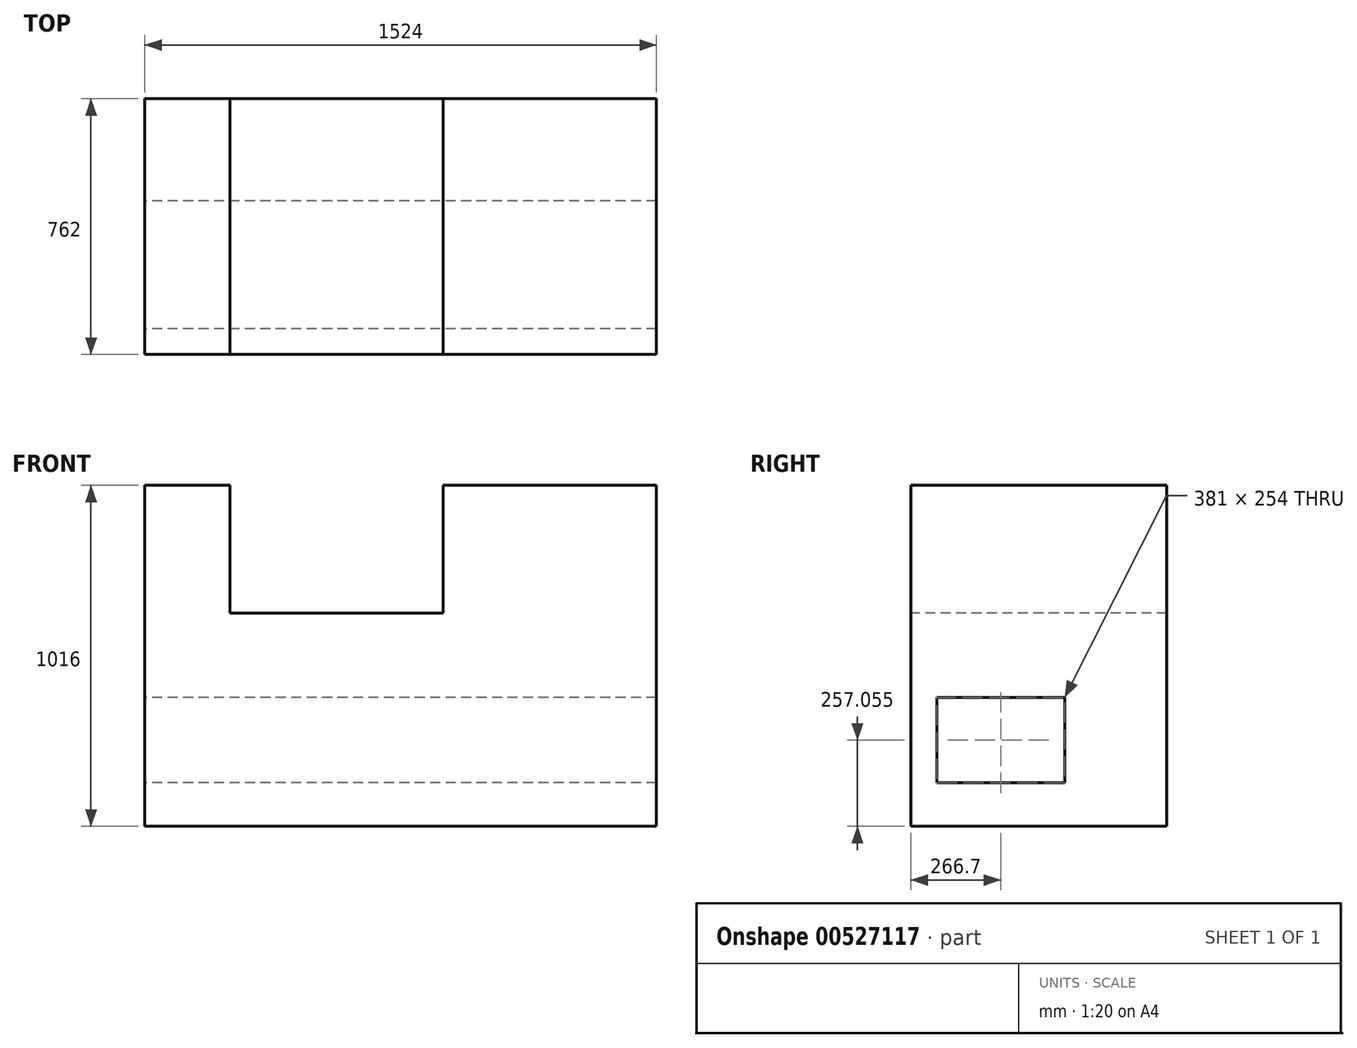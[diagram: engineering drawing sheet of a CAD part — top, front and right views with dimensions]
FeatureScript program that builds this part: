
annotation { "Feature Type Name" : "Feature", "Feature Type Description" : "" }
export const myFeature = defineFeature(function(context is Context, id is Id, definition is map)
    precondition{}
    {
        {
            var Q0;
            Q0=qCreatedBy(makeId("Right.planeOp"),FACE);
            var sketch = newSketch(context, id + "F0", { "sketchPlane" : qUnion([Q0])});
            skLineSegment(sketch, "E0.bottom", {"start": v(-457.2, 536.01) * mm, "end": v(304.8, 536.01) * mm});
            skLineSegment(sketch, "E0.top", {"start": v(-457.2, -479.99) * mm, "end": v(304.8, -479.99) * mm});
            skLineSegment(sketch, "E0.left", {"start": v(-457.2, 536.01) * mm, "end": v(-457.2, -479.99) * mm});
            skLineSegment(sketch, "E0.right", {"start": v(304.8, 536.01) * mm, "end": v(304.8, -479.99) * mm});
            skLineSegment(sketch, "E1.bottom", {"start": v(-381, -349.94) * mm, "end": v(0, -349.94) * mm});
            skLineSegment(sketch, "E1.top", {"start": v(-381, -95.94) * mm, "end": v(0, -95.94) * mm});
            skLineSegment(sketch, "E1.left", {"start": v(-381, -349.94) * mm, "end": v(-381, -95.94) * mm});
            skLineSegment(sketch, "E1.right", {"start": v(0, -349.94) * mm, "end": v(0, -95.94) * mm});
            skSolve(sketch);
        }
        {
            var Q0;
            Q0=makeQuery(id+"F0.imprint","IMPRINT",FACE,{"disambiguationData":[TD([[makeQuery(id+"F0.imprint","IMPRINT",EDGE,{"derivedFrom":sQuery(id+"F0.wireOp",EDGE,"E0.bottom")}),-1.0]])]});
            extrude(context, id + "F1", {"entities" : qUnion([Q0]), "endBound" : BoundingType.SYMMETRIC, "depth" : 1524 * mm});
        }
        {
            var Q0;
            Q0=makeQuery(id+"F1.opExtrude","SWEPT_FACE",FACE,{"disambiguationData":[OSD([sQuery(id+"F0.wireOp",EDGE,"E0.left")])]});
            var sketch = newSketch(context, id + "F2", { "sketchPlane" : qUnion([Q0])});
            skLineSegment(sketch, "E2", {"start": v(-508, 536.01) * mm, "end": v(-508, 155.01) * mm});
            skLineSegment(sketch, "E3", {"start": v(-508, 155.01) * mm, "end": v(127, 155.01) * mm});
            skLineSegment(sketch, "E4", {"start": v(127, 155.01) * mm, "end": v(127, 536.01) * mm});
            skSolve(sketch);
        }
        {
            var Q0;
            {var subQ0=sQuery(id+"F2.wireOp",EDGE,"E2");Q0=makeQuery(id+"F2.imprint","IMPRINT",FACE,{"disambiguationData":[TD([[makeQuery(id+"F2.imprint","IMPRINT",EDGE,{"derivedFrom":subQ0}),1.0]])]});}
            extrude(context, id + "F3", {"entities" : qUnion([Q0]), "operationType" : NewBodyOperationType.REMOVE, "endBound" : BoundingType.SYMMETRIC, "oppositeDirection" : true, "depth" : 27940 * mm});
        }
    });
